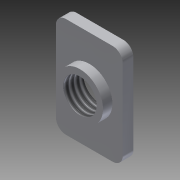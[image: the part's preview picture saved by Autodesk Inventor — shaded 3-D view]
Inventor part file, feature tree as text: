
AUTODESK INVENTOR PART (.ipt)
format: ipt  version: 2014 SP1 (Build 180222100, 222)  size: 104,448 bytes
history: native  units: in
note: dims shown in document units (in); Inventor stores cm internally (conversion verified against a paired STEP export)
features: extrude x2, sketch x2, thread x1, fillet x1
ambient origin geometry x8: Origin, YZ Plane, XZ Plane, XY Plane, X Axis, Y Axis, Z Axis, Center Point
bodies: Solid1 (feature_tree)
feature tree (6):
  extrude  "Extrusion1"  Depth=0.3937in
  extrude  "Extrusion2"  Depth=0.063in TaperAngle=0.0deg
  thread  "Thread1"  [1 undecoded]
  fillet  "Fillet1"  Radius=0.0551in
  sketch  "Sketch1"  dims[d0=0.5906in d1=0.3937in]
  sketch  "Sketch2"  dims[d2=0.1969in d3=0.063in d4=0.0in d5=0.2717in d6=0.0551in d7=0.0in d8=0.3937in d9=0.0in d10=0.0591in]
note: 1 required parameter value undecoded (feature->parameter linkage not recoverable at this tier; creation-order binding heuristic only, values carry confidence <= 0.55)
